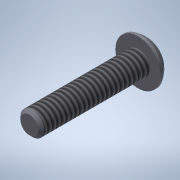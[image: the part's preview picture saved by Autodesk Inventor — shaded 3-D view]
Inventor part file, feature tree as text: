
AUTODESK INVENTOR PART (.ipt)
format: ipt  version: 2020 (Build 240168000, 168)  size: 135,680 bytes
history: native  units: in
note: dims shown in document units (in); Inventor stores cm internally (conversion verified against a paired STEP export)
features: sketch x3, extrude x2, revolve x1, chamfer x1, thread x1
ambient origin geometry x8: Origin, YZ Plane, XZ Plane, XY Plane, X Axis, Y Axis, Z Axis, Center Point
bodies: Solid1 (feature_tree)
feature tree (8):
  extrude  "Extrusion1"  Depth=0.75in TaperAngle=0.0deg
  revolve  "Revolution1"  [1 undecoded]
  extrude  "Extrusion2"  Depth=0.0938in
  chamfer  "Chamfer1"  Distance=0.0625in
  thread  "Thread1"  [1 undecoded]
  sketch  "Sketch1"  dims[d0=0.164in d1=0.75in d2=0.0in]
  sketch  "Sketch2"  dims[d3=0.087in d6=0.08in]
  sketch  "Sketch3"  dims[d7=90.0deg d8=0.0938in d9=0.0625in d10=0.0in d13=0.02in d14=0.125in d15=45.0deg d16=1.0in d17=0.0in d19=0.156in]
note: 2 required parameter values undecoded (feature->parameter linkage not recoverable at this tier; creation-order binding heuristic only, values carry confidence <= 0.55)